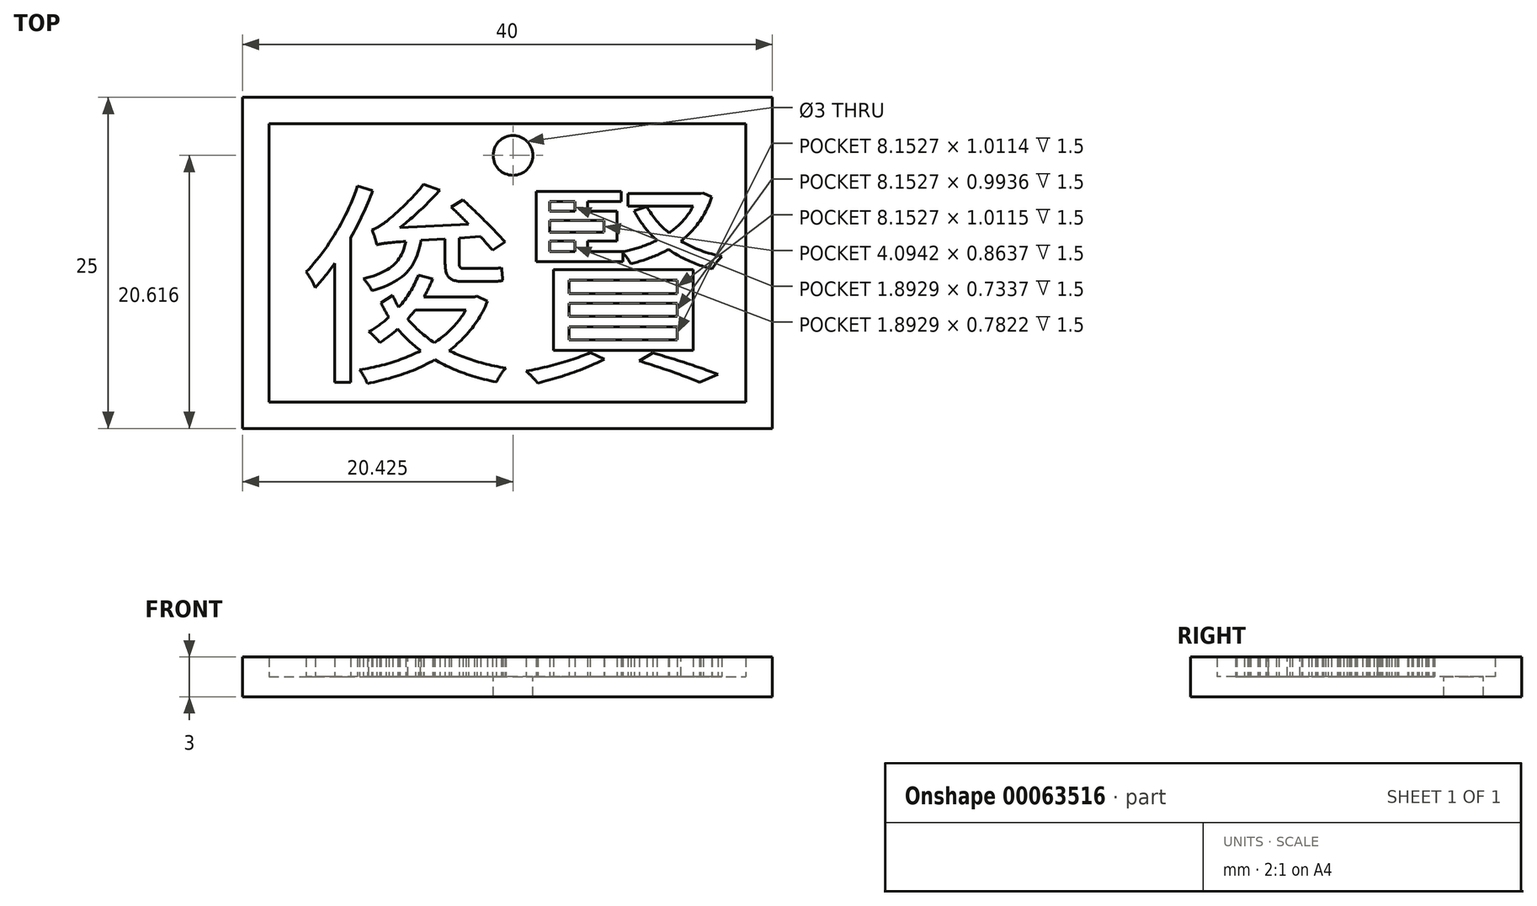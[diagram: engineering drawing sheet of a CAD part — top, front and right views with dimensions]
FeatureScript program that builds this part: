
annotation { "Feature Type Name" : "Feature", "Feature Type Description" : "" }
export const myFeature = defineFeature(function(context is Context, id is Id, definition is map)
    precondition{}
    {
        {
            var Q0;
            Q0=qCreatedBy(makeId("Top.planeOp"),FACE);
            var sketch = newSketch(context, id + "F0", { "sketchPlane" : qUnion([Q0])});
            skLineSegment(sketch, "E0.bottom", {"start": v(-32.96, 29.3) * mm, "end": v(7.04, 29.3) * mm});
            skLineSegment(sketch, "E0.top", {"start": v(-32.96, 4.3) * mm, "end": v(7.04, 4.3) * mm});
            skLineSegment(sketch, "E0.left", {"start": v(-32.96, 29.3) * mm, "end": v(-32.96, 4.3) * mm});
            skLineSegment(sketch, "E0.right", {"start": v(7.04, 29.3) * mm, "end": v(7.04, 4.3) * mm});
            skSolve(sketch);
        }
        {
            var Q0;
            Q0 = qSketchRegion(id + "F0", true);
            extrude(context, id + "F1", {"entities" : qUnion([Q0]), "depth" : 1.5 * mm});
        }
        {
            var Q0;
            Q0=makeQuery(id+"F1.opExtrude","CAP_FACE",FACE,{"disambiguationData":[OSD([sQuery(id+"F0.wireOp",EDGE,"E0.bottom"),sQuery(id+"F0.wireOp",EDGE,"E0.top"),sQuery(id+"F0.wireOp",EDGE,"E0.left"),sQuery(id+"F0.wireOp",EDGE,"E0.right")])],"isStart":false});
            var sketch = newSketch(context, id + "F2", { "sketchPlane" : qUnion([Q0])});
            skLineSegment(sketch, "E1.bottom", {"start": v(-32.96, 29.3) * mm, "end": v(7.04, 29.3) * mm});
            skLineSegment(sketch, "E1.top", {"start": v(-32.96, 4.3) * mm, "end": v(7.04, 4.3) * mm});
            skLineSegment(sketch, "E1.left", {"start": v(-32.96, 29.3) * mm, "end": v(-32.96, 4.3) * mm});
            skLineSegment(sketch, "E1.right", {"start": v(7.04, 29.3) * mm, "end": v(7.04, 4.3) * mm});
            skLineSegment(sketch, "E2.0", {"start": v(-30.96, 27.3) * mm, "end": v(5.04, 27.3) * mm});
            skLineSegment(sketch, "E2.1", {"start": v(-30.96, 27.3) * mm, "end": v(-30.96, 6.3) * mm});
            skLineSegment(sketch, "E2.2", {"start": v(-30.96, 6.3) * mm, "end": v(5.04, 6.3) * mm});
            skLineSegment(sketch, "E2.3", {"start": v(5.04, 27.3) * mm, "end": v(5.04, 6.3) * mm});
            skSolve(sketch);
        }
        {
            var Q0;
            Q0 = qSketchRegion(id + "F2", true);
            extrude(context, id + "F3", {"entities" : qUnion([Q0]), "operationType" : NewBodyOperationType.ADD, "depth" : 1.5 * mm});
        }
        {
            var Q0;
            Q0=makeQuery(id+"F1.opExtrude","CAP_FACE",FACE,{"disambiguationData":[OSD([sQuery(id+"F0.wireOp",EDGE,"E0.bottom"),sQuery(id+"F0.wireOp",EDGE,"E0.top"),sQuery(id+"F0.wireOp",EDGE,"E0.left"),sQuery(id+"F0.wireOp",EDGE,"E0.right")])],"isStart":false});
            var sketch = newSketch(context, id + "F4", { "sketchPlane" : qUnion([Q0])});
            skText(sketch, "E3", { "text": "俊賢", "fontName": "NotoSansCJKtc-Regular.otf"});
            const initialGuessF4  = {"E3": [-0.02878, 0.00902, 1, 0, 0.01174]};
            skSetInitialGuess(sketch, initialGuessF4);
            skSolve(sketch);
        }
        {
            var Q0;
            Q0 = qSketchRegion(id + "F4", true);
            extrude(context, id + "F5", {"entities" : qUnion([Q0]), "operationType" : NewBodyOperationType.ADD, "depth" : 1.5 * mm});
        }
        {
            var Q0;
            Q0=makeQuery(id+"F5.boolean.opBoolean","SPLIT",FACE,{"disambiguationData":[TD([makeQuery(id+"F3.opExtrude","SWEPT_FACE",FACE,{"disambiguationData":[OSD([sQuery(id+"F2.wireOp",EDGE,"E2.0")])]})])],"derivedFrom":makeQuery(id+"F1.opExtrude","CAP_FACE",FACE,{"disambiguationData":[OSD([sQuery(id+"F0.wireOp",EDGE,"E0.bottom"),sQuery(id+"F0.wireOp",EDGE,"E0.top"),sQuery(id+"F0.wireOp",EDGE,"E0.left"),sQuery(id+"F0.wireOp",EDGE,"E0.right")])],"isStart":false})});
            var sketch = newSketch(context, id + "F6", { "sketchPlane" : qUnion([Q0])});
            skCircle(sketch, "E4", {"center": v(-12.54, 24.92) * mm, "radius": 1.5 * mm});
            skSolve(sketch);
        }
        {
            var Q0;
            Q0=makeQuery(id+"F6.imprint","IMPRINT",FACE,{"disambiguationData":[TD([[makeQuery(id+"F6.imprint","IMPRINT",EDGE,{"derivedFrom":sQuery(id+"F6.wireOp",EDGE,"E4")}),1.0]])]});
            extrude(context, id + "F7", {"entities" : qUnion([Q0]), "operationType" : NewBodyOperationType.REMOVE, "oppositeDirection" : true, "depth" : 25 * mm});
        }
    });
